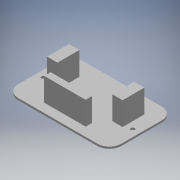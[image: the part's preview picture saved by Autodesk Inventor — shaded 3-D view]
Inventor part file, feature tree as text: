
AUTODESK INVENTOR PART (.ipt)
format: ipt  version: 2017 (Build 210142000, 142)  size: 152,576 bytes
history: native  units: in
note: dims shown in document units (in); Inventor stores cm internally (conversion verified against a paired STEP export)
features: sketch x4, other x3, extrude x1
ambient origin geometry x8: Origin, YZ Plane, XZ Plane, XY Plane, X Axis, Y Axis, Z Axis, Center Point
bodies: Solid1 (feature_tree)
feature tree (8):
  other  "capaservo.ipt"
  extrude  "Extrusion1"  Depth=0.3937in
  other  "Solid1::capaservo.ipt"
  other  "TaggingFeature1"
  sketch  "Sketch1"  dims[d0=0.3937in d1=0.1181in]
  sketch  "Sketch2"  dims[d2=2.1063in d3=0.0in]
  sketch  "Sketch3"
  sketch  "Sketch4"
